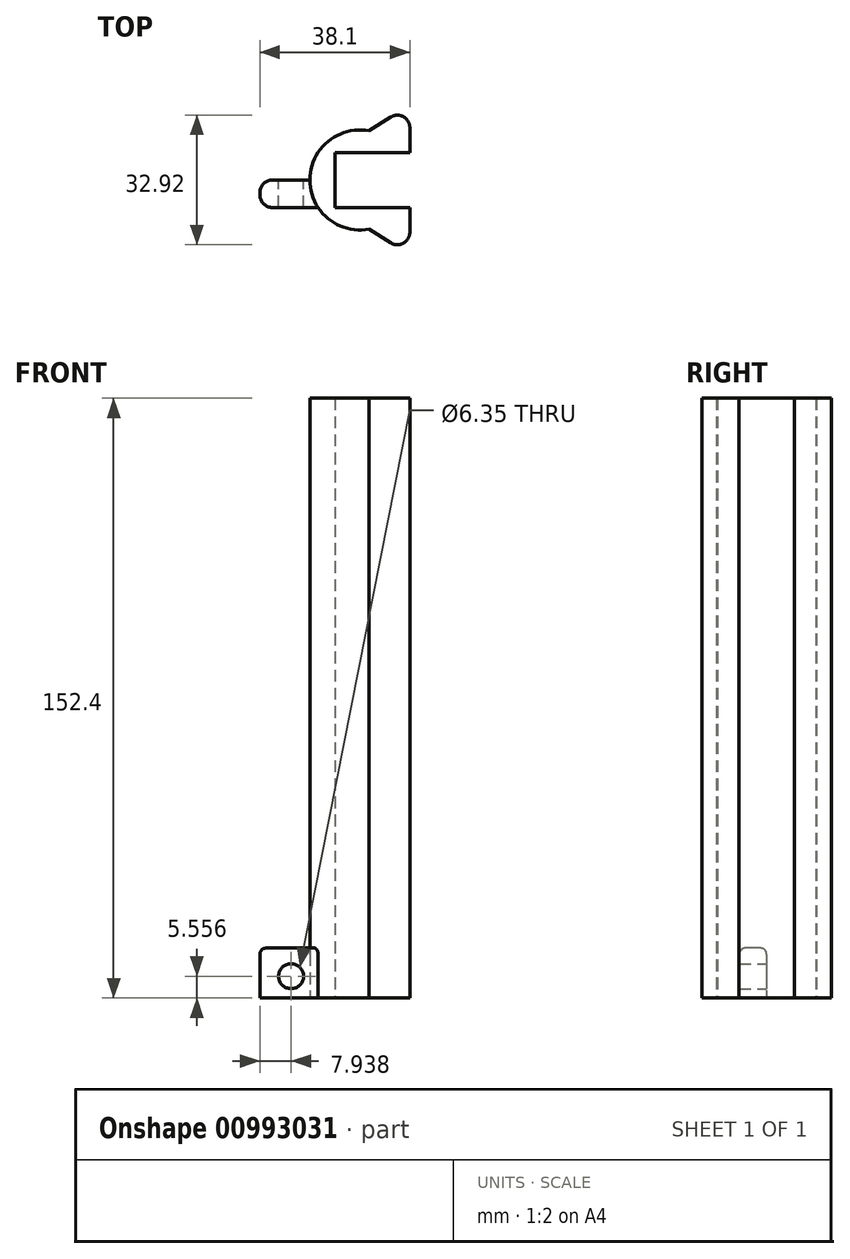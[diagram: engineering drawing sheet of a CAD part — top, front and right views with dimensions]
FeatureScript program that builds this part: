
annotation { "Feature Type Name" : "Feature", "Feature Type Description" : "" }
export const myFeature = defineFeature(function(context is Context, id is Id, definition is map)
    precondition{}
    {
        {
            var Q0;
            Q0=qCreatedBy(makeId("Top.planeOp"),FACE);
            var sketch = newSketch(context, id + "F0", { "sketchPlane" : qUnion([Q0])});
            skCircle(sketch, "E0", {"center": v(0, 0) * mm, "radius": 12.7 * mm});
            skLineSegment(sketch, "E1.bottom", {"start": v(31.75, -6.99) * mm, "end": v(-6.35, -6.99) * mm});
            skLineSegment(sketch, "E1.top", {"start": v(31.75, 6.99) * mm, "end": v(-6.35, 6.99) * mm});
            skLineSegment(sketch, "E1.left", {"start": v(31.75, -6.98) * mm, "end": v(31.75, 6.99) * mm});
            skLineSegment(sketch, "E1.right", {"start": v(-6.35, -6.98) * mm, "end": v(-6.35, 6.99) * mm});
            skPoint(sketch, "E1.middle", {"position": v(12.7, 0) * mm});
            skLineSegment(sketch, "E2.bottom", {"start": v(0, 0) * mm, "end": v(-25.4, 0) * mm});
            skLineSegment(sketch, "E2.top", {"start": v(0, -6.99) * mm, "end": v(-25.4, -6.99) * mm});
            skLineSegment(sketch, "E2.left", {"start": v(0, 0) * mm, "end": v(0, -6.99) * mm});
            skLineSegment(sketch, "E2.right", {"start": v(-25.4, 0) * mm, "end": v(-25.4, -6.98) * mm});
            skLineSegment(sketch, "E3", {"start": v(12.7, 0) * mm, "end": v(12.7, 13.28) * mm});
            skLineSegment(sketch, "E4", {"start": v(12.7, 19.05) * mm, "end": v(12.7, 0) * mm, "construction": true});
            skLineSegment(sketch, "E5", {"start": v(12.7, 0) * mm, "end": v(12.7, -13.28) * mm});
            skLineSegment(sketch, "E6", {"start": v(-6.35, -6.99) * mm, "end": v(7.83, -15.96) * mm});
            skLineSegment(sketch, "E7", {"start": v(-6.35, 6.99) * mm, "end": v(7.83, 15.96) * mm});
            skPoint(sketch, "E8.visualSharp", {"position": v(12.7, -19.05) * mm});
            skArc(sketch, "E8.filletArc", {"start": v(7.83, -15.96) * mm, "mid": v(11.06, -16.06) * mm, "end": v(12.7, -13.28) * mm});
            skPoint(sketch, "E9.visualSharp", {"position": v(12.7, 19.05) * mm});
            skArc(sketch, "E9.filletArc", {"start": v(12.7, 13.28) * mm, "mid": v(11.06, 16.06) * mm, "end": v(7.83, 15.96) * mm});
            skSolve(sketch);
        }
        {
            var Q0;
            {var subQ5=sQuery(id+"F0.wireOp",EDGE,"E1.right");Q0=makeQuery(id+"F0.imprint","IMPRINT",FACE,{"disambiguationData":[TD([[makeQuery(id+"F0.imprint","IMPRINT",EDGE,{"derivedFrom":subQ5}),1.0]])]});}
            var Q1;
            {var subQ0=sQuery(id+"F0.wireOp",EDGE,"f76607b9-ebd7-49f0-a940-a296c7770240.bottom");var subQ1=sQuery(id+"F0.wireOp",EDGE,"E0");var subQ2=makeQuery(id+"F0.imprint","INTERSECT",VERTEX,{"derivedFrom":[subQ1,subQ0]});Q1=makeQuery(id+"F0.imprint","IMPRINT",FACE,{"disambiguationData":[TD([[makeQuery(id+"F0.imprint","IMPRINT",EDGE,{"disambiguationData":[TD([[subQ2,-1.0]])],"derivedFrom":subQ1}),1.0]])]});}
            var Q2;
            {var subQ0=sQuery(id+"F0.wireOp",EDGE,"E6");var subQ1=sQuery(id+"F0.wireOp",EDGE,"E0");var subQ2=makeQuery(id+"F0.imprint","INTERSECT",VERTEX,{"derivedFrom":[subQ1,subQ0]});Q2=makeQuery(id+"F0.imprint","IMPRINT",FACE,{"disambiguationData":[TD([[makeQuery(id+"F0.imprint","IMPRINT",EDGE,{"disambiguationData":[TD([[subQ2,-1.0]])],"derivedFrom":subQ1}),1.0]])]});}
            var Q3;
            {var subQ0=sQuery(id+"F0.wireOp",EDGE,"E6");var subQ1=sQuery(id+"F0.wireOp",EDGE,"E0");var subQ2=makeQuery(id+"F0.imprint","INTERSECT",VERTEX,{"derivedFrom":[subQ1,subQ0]});Q3=makeQuery(id+"F0.imprint","IMPRINT",FACE,{"disambiguationData":[TD([[makeQuery(id+"F0.imprint","IMPRINT",EDGE,{"disambiguationData":[TD([[subQ2,-1.0]])],"derivedFrom":subQ1}),-1.0]])]});}
            var Q4;
            {var subQ0=sQuery(id+"F0.wireOp",EDGE,"E7");var subQ1=sQuery(id+"F0.wireOp",EDGE,"E0");var subQ2=makeQuery(id+"F0.imprint","INTERSECT",VERTEX,{"derivedFrom":[subQ1,subQ0]});Q4=makeQuery(id+"F0.imprint","IMPRINT",FACE,{"disambiguationData":[TD([[makeQuery(id+"F0.imprint","IMPRINT",EDGE,{"disambiguationData":[TD([[subQ2,1.0]])],"derivedFrom":subQ1}),-1.0]])]});}
            extrude(context, id + "F1", {"entities" : qUnion([Q0, Q1, Q2, Q3, Q4]), "depth" : 152.4 * mm, "offsetDistance" : 25.4 * mm});
        }
        {
            var Q0;
            {var subQ5=sQuery(id+"F0.wireOp",EDGE,"E1.right");Q0=makeQuery(id+"F0.imprint","IMPRINT",FACE,{"disambiguationData":[TD([[makeQuery(id+"F0.imprint","IMPRINT",EDGE,{"derivedFrom":subQ5}),1.0]])]});}
            var Q1;
            {var subQ0=sQuery(id+"F0.wireOp",EDGE,"f76607b9-ebd7-49f0-a940-a296c7770240.bottom");var subQ1=sQuery(id+"F0.wireOp",EDGE,"E0");var subQ2=makeQuery(id+"F0.imprint","INTERSECT",VERTEX,{"derivedFrom":[subQ1,subQ0]});Q1=makeQuery(id+"F0.imprint","IMPRINT",FACE,{"disambiguationData":[TD([[makeQuery(id+"F0.imprint","IMPRINT",EDGE,{"disambiguationData":[TD([[subQ2,-1.0]])],"derivedFrom":subQ1}),1.0]])]});}
            var Q2;
            {var subQ5=sQuery(id+"F0.wireOp",EDGE,"E2.right");Q2=makeQuery(id+"F0.imprint","IMPRINT",FACE,{"disambiguationData":[TD([[makeQuery(id+"F0.imprint","IMPRINT",EDGE,{"derivedFrom":subQ5}),1.0]])]});}
            extrude(context, id + "F2", {"entities" : qUnion([Q0, Q1, Q2]), "operationType" : NewBodyOperationType.ADD, "depth" : 12.7 * mm, "offsetDistance" : 25.4 * mm});
        }
        {
            var Q0;
            Q0=makeQuery(id+"F2.opExtrude","SWEPT_EDGE",EDGE,{"disambiguationData":[OSD([sQuery(id+"F0.wireOp",EDGE,"E2.bottom"),sQuery(id+"F0.wireOp",EDGE,"E2.right")])]});
            var Q1;
            Q1=makeQuery(id+"F2.opExtrude","SWEPT_EDGE",EDGE,{"disambiguationData":[OSD([sQuery(id+"F0.wireOp",EDGE,"E2.top"),sQuery(id+"F0.wireOp",EDGE,"E2.right")])]});
            fillet(context, id + "F3", {"entities" : qUnion([Q0, Q1]), "radius" : 3.17 * mm, "tangentPropagation" : true, "allowEdgeOverflow" : false});
        }
        {
            var Q0;
            Q0=makeQuery(id+"F2.opExtrude","CAP_EDGE",EDGE,{"disambiguationData":[OSD([sQuery(id+"F0.wireOp",EDGE,"E2.bottom")])],"isStart":false});
            fillet(context, id + "F4", {"entities" : qUnion([Q0]), "radius" : 1.59 * mm, "tangentPropagation" : true, "allowEdgeOverflow" : false});
        }
        {
            var Q0;
            Q0=makeQuery(id+"F2.opExtrude","SWEPT_FACE",FACE,{"disambiguationData":[OSD([sQuery(id+"F0.wireOp",EDGE,"E2.bottom")])]});
            var sketch = newSketch(context, id + "F5", { "sketchPlane" : qUnion([Q0])});
            skLineSegment(sketch, "E10", {"start": v(12.7, 11.11) * mm, "end": v(22.23, 0) * mm, "construction": true});
            skCircle(sketch, "E11", {"center": v(17.46, 5.56) * mm, "radius": 3.18 * mm});
            skSolve(sketch);
        }
        {
            var Q0;
            Q0=makeQuery(id+"F5.imprint","IMPRINT",FACE,{"disambiguationData":[TD([[makeQuery(id+"F5.imprint","IMPRINT",EDGE,{"derivedFrom":sQuery(id+"F5.wireOp",EDGE,"E11")}),1.0]])]});
            extrude(context, id + "F6", {"entities" : qUnion([Q0]), "operationType" : NewBodyOperationType.REMOVE, "oppositeDirection" : true, "depth" : 25.4 * mm, "offsetDistance" : 25.4 * mm});
        }
    });
